# Revit family: CADS_AIRFLOWdev_Fan_iCON15S_eco
name_source: partatom
category: Mechanical Equipment
revit_build: Autodesk Revit 2015 (Build: 20160512_1515(x64)
units: mm (PartAtom-declared; Revit-internal decimal feet)

## types (1)
- iC eco 15S
    6MonthlyMaintenance = Visually inspect system, clean the fan and ducting if necessary
    A = 197 mm
    AccessClearanceBottom = 350 mm
    AccessClearanceFront = 350 mm
    AccessClearanceLeft = 350 mm
    AccessClearanceRear = 0 mm  [stored 0 ft]
    AccessClearanceRight = 350 mm
    AccessClearanceTop = 350 mm
    AnthraciteFT = CADS_AIRFLOWdev_Fan_iCON15_Covers : Anthracite
    AssemblyPlace = UKNOWN
    AssetType = Fixed
    BMSLinks = No
    Body = CADS_AirFlow_White
    C = 68 mm
    CADS_Index = 0
    CEApproval = Yes
    Category = Pr_65_67_29_05:Axial Flow Fans
    ChromeFT = CADS_AIRFLOWdev_Fan_iCON15_Covers : Chrome
    Color = White
(optional Anthracite (52634503), Sandstone (52634505), Chrome (52634502) and Silver (52634504) covers are available)
    Controls = Basic on/off functionality controlled by external switch.
The following additional, interchangeable modules can be fitted to the iCON 15S:
Pull cord (72573603)
Pull cord with adjustable timer (72574204)
Humidity, Pull Cord with Timer overrun (72574202)
Motion Sensor with Timer overrun (72574203)
Motion sensor/humidity/timer (72574201)
Delay start timer with pull cord (72682307)
    D = 100 mm  [stored 0.328084 ft]
    DTFT = iCON15S_Eco_Modules : Delayed Timer With Pull Cord
    Default Elevation = 1219 mm
    Description = An intermittent SELV extract fan with interchangeable modular controls and covers and a Red Dot Design Award winner
    DesignOfDomesticVentilation = This fan should provide the minimum flow rates outlined and installed in line with Approved Document Part F of the Building Regulations.
    Ductwork = 100mm flexible or rigid
    DurationUnit = Year
    E = 40 mm  [stored 0.131234 ft]
    ErPEnergyRating = C
    ErPFiche = https://www.airflow.com
    Exclusions = Hasn't been installed or used in accordance with the instructions
Connected with an unsuitable electrical supply
Has been misused, neglected or damaged
Modified or repaired by someone not authorised by Airflow Developments Ltd
Hasn't been installed according to Building Regulations or IEEE wiring regulations
    ExpectedServiceLife = 3
    ExternalExhaustAirTerminals = 90% free air grille
    Fan = Low voltage domestic intermittent extract fan
    Features = Low energy axial fan
Up to 22l/sec flow rate
Stylish design with unique iris shutter
Interchangeable modular controls and interchangeable covers
IPX4 rated
Sound levels from just 30.3dB(A)
Red Dot Design Award Winner
    Finish = Matte
    FireControlPanelLinks = No
    GlobalTradeItemNumber = 5019009307657
    Grade = Virgin
    GrossWeight = 0.74 kg
    HPCFT = iCON15S_Eco_Modules : Humidity Pull Cord With Timer Overrun
    HasPartWinding = Yes
    HasProtectiveEarth = No
    IP_Code = IPX4
    ISO140001 = Yes
    ISO90001 = Yes
    IfcExportAs = IfcFanType
    IfcExportType = NOTDEFINED
    InsulationStandardClass = Double Insulated
    IsExtendedWarranty = No
    IsGuarded = Yes
    MSHFT = iCON15S_Eco_Modules : Motion Sensor Humidity Timer
    MSTFT = iCON15S_Eco_Modules : Motion Sensor With Timer Overrun
    Manufacturer = Airflow Developments Ltd
    ManufacturerAddress = Aidelle House
Lancaster Road
Cressex Business Park
High Wycombe
Bucks
HP123QP
    ManufacturerTelephone = 01494 525252
    ManufacturerWebsite = www.airflow.com
    Material = Plastic
    ModelLabel = iCON 15S
    ModelReference = 72683701
    MotorDriveType = Direct Drive
    MotorEnclosureType = Totally Enclosed Air Over
    NBSCode = 90-45-30/310 Axial flow fans;
    NominalAirFlowRate = 22.0 L/s
    NominalFrequencyRange = 50-60
    NominalHeight = 197 mm
    NominalLength = 85 mm
    NominalPowerRate = 8 W
    NominalRotationSpeed = 45 Hz
    NominalStaticPressure = 35.0 Pa
    NominalWidth = 197 mm
    NumberOfPoles = 1
    OperationAndMaintenanceManual = https://www.airflow.com
    OperationAndMaintenanceManualAccessories = https://www.airflow.com
    OperationTemperatureRange = up to 40°C
    PCAFT = iCON15S_Eco_Modules : Pull Cord Adjustible Timer
    PCFT = iCON15S_Eco_Modules : Pull Cord
    PointOfContact = Airflow Developments Ltd
    PowerSource = System-powered
    PressureCurve = https://www.airflow.com
    ProductLiterature = https://www.airflow.com
    ProductLiteratureAccessories = https://www.airflow.com
    ProductionYear = 2017
    Quantity = 1
    QuietMarkApproval = No
    RatedCurrent = 3 A
    RatedVoltage = 12 V
    RedDotDesignAward = Yes
    ReplacementCost = 183.984
    RoomExtractAirTerminalDevices = Low voltage en-suite, toilet and bathroom fan
    SandstoneFT = CADS_AIRFLOWdev_Fan_iCON15_Covers : Standstone
    ServiceLifeDuration = 3
    ServiceLifeType = ExpectedServiceLife
    Shape = Round
    ShippingWeight = 1.15 kg
    SilverFT = CADS_AIRFLOWdev_Fan_iCON15_Covers : Silver
    Size = 85 x 197 x 197
    StartingTime = 5.0 s
    Status = New
    SupplyPhase = 1
    Type = iC eco 15S
    Uniclass2015 = Pr_65_67_29_05
    WarrantyContent = Covered against faulty material or workmanship - not reinstallation if needed
    WarrantyGuarantor = Airflow Developments Ltd
    WarrantyPeriod = 2
    WarrantyPeriodForMotors = 1
    WarrantyPeriodWhenRegistered = 3

note: [stored X ft] marks values corroborated as IEEE doubles in the binary element streams (Revit-internal decimal feet)

## geometry (parser evidence)
native form markers: Blend x4, Sweep x9
no freeform markers — native parametric forms only
